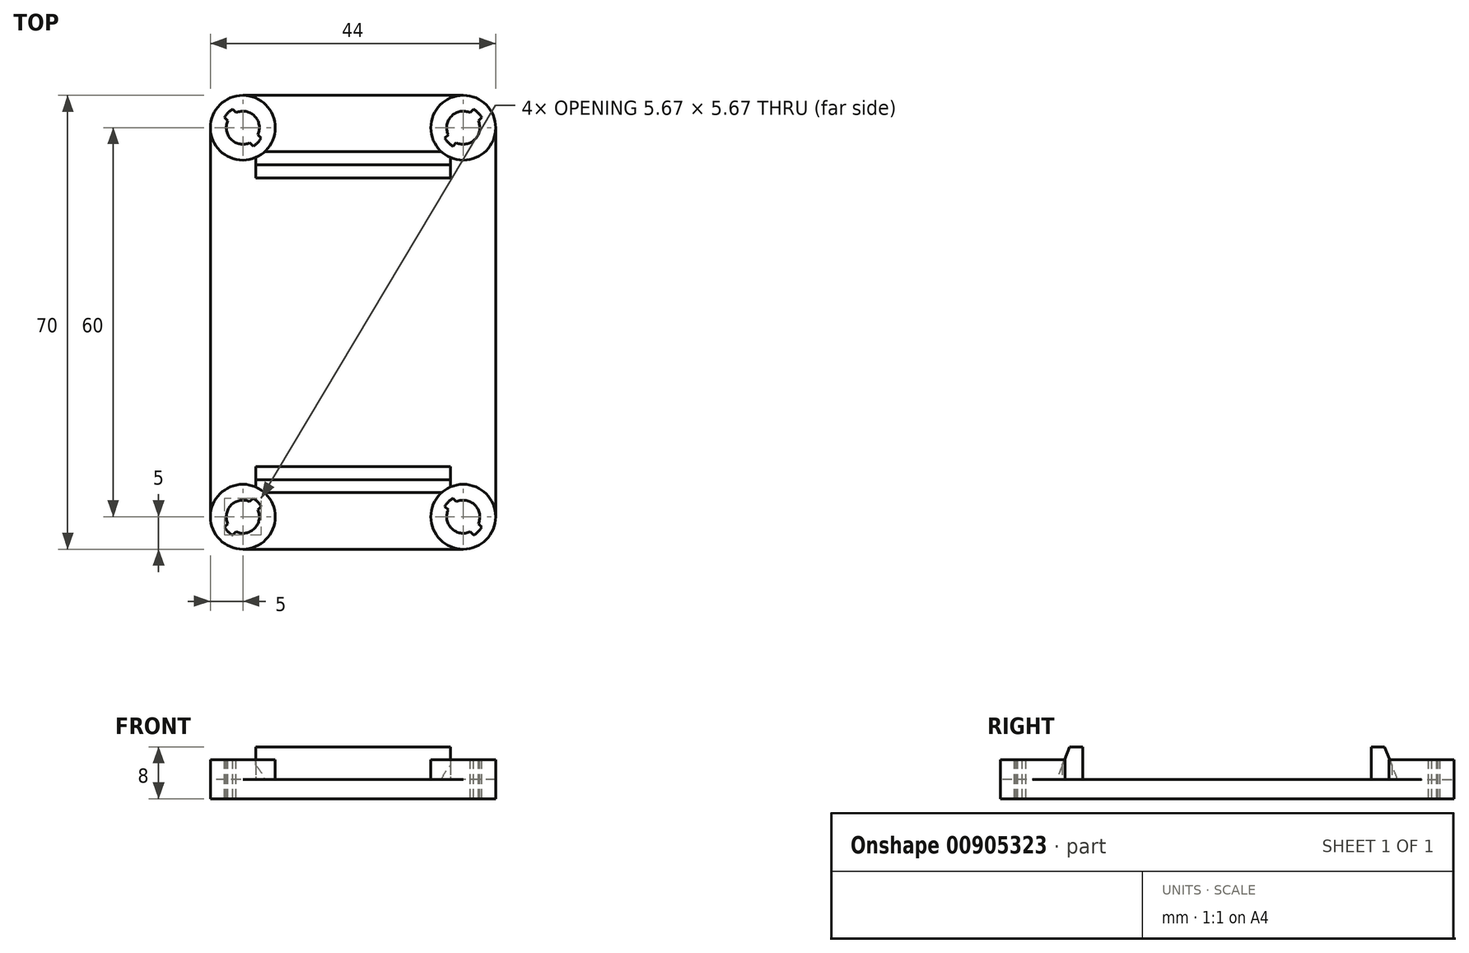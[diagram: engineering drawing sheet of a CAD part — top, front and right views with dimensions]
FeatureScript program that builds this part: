
annotation { "Feature Type Name" : "Feature", "Feature Type Description" : "" }
export const myFeature = defineFeature(function(context is Context, id is Id, definition is map)
    precondition{}
    {
        {
            var Q0;
            Q0=qCreatedBy(makeId("Top.planeOp"),FACE);
            var sketch = newSketch(context, id + "F0", { "sketchPlane" : qUnion([Q0])});
            skLineSegment(sketch, "E0.bottom", {"start": v(32.5, -22) * mm, "end": v(-32.5, -22) * mm, "construction": true});
            skLineSegment(sketch, "E0.top", {"start": v(32.5, 22) * mm, "end": v(-32.5, 22) * mm, "construction": true});
            skLineSegment(sketch, "E0.left", {"start": v(32.5, -22) * mm, "end": v(32.5, 22) * mm, "construction": true});
            skLineSegment(sketch, "E0.right", {"start": v(-32.5, -22) * mm, "end": v(-32.5, 22) * mm, "construction": true});
            skPoint(sketch, "E0.middle", {"position": v(0, 0) * mm});
            skLineSegment(sketch, "E1.bottom", {"start": v(17, -30) * mm, "end": v(-17, -30) * mm, "construction": true});
            skLineSegment(sketch, "E1.top", {"start": v(17, 30) * mm, "end": v(-17, 30) * mm, "construction": true});
            skLineSegment(sketch, "E1.left", {"start": v(17, -30) * mm, "end": v(17, 30) * mm, "construction": true});
            skLineSegment(sketch, "E1.right", {"start": v(-17, -30) * mm, "end": v(-17, 30) * mm, "construction": true});
            skLineSegment(sketch, "E2.0", {"start": v(17, 35) * mm, "end": v(-17, 35) * mm});
            skLineSegment(sketch, "E2.1", {"start": v(22, -30) * mm, "end": v(22, 30) * mm});
            skLineSegment(sketch, "E2.2", {"start": v(17, -35) * mm, "end": v(-17, -35) * mm});
            skLineSegment(sketch, "E2.3", {"start": v(-22, -30) * mm, "end": v(-22, 30) * mm});
            skPoint(sketch, "E3.visualSharp", {"position": v(-22, 35) * mm});
            skArc(sketch, "E3.filletArc", {"start": v(-17, 35) * mm, "mid": v(-20.54, 33.54) * mm, "end": v(-22, 30) * mm});
            skPoint(sketch, "E4.visualSharp", {"position": v(22, 35) * mm});
            skArc(sketch, "E4.filletArc", {"start": v(22, 30) * mm, "mid": v(20.54, 33.54) * mm, "end": v(17, 35) * mm});
            skPoint(sketch, "E5.visualSharp", {"position": v(22, -35) * mm});
            skArc(sketch, "E5.filletArc", {"start": v(17, -35) * mm, "mid": v(20.54, -33.54) * mm, "end": v(22, -30) * mm});
            skPoint(sketch, "E6.visualSharp", {"position": v(-22, -35) * mm});
            skArc(sketch, "E6.filletArc", {"start": v(-22, -30) * mm, "mid": v(-20.54, -33.54) * mm, "end": v(-17, -35) * mm});
            skSolve(sketch);
        }
        {
            var Q0;
            Q0 = qSketchRegion(id + "F0", true);
            extrude(context, id + "F1", {"entities" : qUnion([Q0]), "depth" : 3 * mm, "offsetDistance" : 25 * mm});
        }
        {
            var Q0;
            Q0=qCreatedBy(makeId("Top.planeOp"),FACE);
            var sketch = newSketch(context, id + "F2", { "sketchPlane" : qUnion([Q0])});
            skLineSegment(sketch, "E7.bottom", {"start": v(32.5, -22) * mm, "end": v(-32.5, -22) * mm, "construction": true});
            skLineSegment(sketch, "E7.top", {"start": v(32.5, 22) * mm, "end": v(-32.5, 22) * mm, "construction": true});
            skLineSegment(sketch, "E7.left", {"start": v(32.5, -22) * mm, "end": v(32.5, 22) * mm, "construction": true});
            skLineSegment(sketch, "E7.right", {"start": v(-32.5, -22) * mm, "end": v(-32.5, 22) * mm, "construction": true});
            skPoint(sketch, "E7.middle", {"position": v(0, 0) * mm});
            skLineSegment(sketch, "E8.bottom", {"start": v(17, -30) * mm, "end": v(-17, -30) * mm, "construction": true});
            skLineSegment(sketch, "E8.top", {"start": v(17, 30) * mm, "end": v(-17, 30) * mm, "construction": true});
            skLineSegment(sketch, "E8.left", {"start": v(17, -30) * mm, "end": v(17, 30) * mm, "construction": true});
            skLineSegment(sketch, "E8.right", {"start": v(-17, -30) * mm, "end": v(-17, 30) * mm, "construction": true});
            skLineSegment(sketch, "E9.0", {"start": v(22, 35) * mm, "end": v(-22, 35) * mm});
            skLineSegment(sketch, "E9.1", {"start": v(22, -35) * mm, "end": v(22, 35) * mm});
            skLineSegment(sketch, "E9.2", {"start": v(22, -35) * mm, "end": v(-22, -35) * mm});
            skLineSegment(sketch, "E9.3", {"start": v(-22, -35) * mm, "end": v(-22, 35) * mm});
            skCircle(sketch, "E10", {"center": v(-17, -30) * mm, "radius": 5 * mm});
            skCircle(sketch, "E11", {"center": v(17, -30) * mm, "radius": 5 * mm});
            skCircle(sketch, "E12", {"center": v(17, 30) * mm, "radius": 5 * mm});
            skCircle(sketch, "E13", {"center": v(-17, 30) * mm, "radius": 5 * mm});
            skSolve(sketch);
        }
        {
            var Q0;
            {var subQ0=sQuery(id+"F2.wireOp",EDGE,"E13");var subQ1=makeQuery(id+"F2.imprint","INTERSECT",VERTEX,{"derivedFrom":[sQuery(id+"F2.wireOp",EDGE,"E9.0"),subQ0]});Q0=makeQuery(id+"F2.imprint","IMPRINT",FACE,{"disambiguationData":[TD([[makeQuery(id+"F2.imprint","IMPRINT",EDGE,{"disambiguationData":[TD([[subQ1,-1.0]])],"derivedFrom":subQ0}),1.0]])]});}
            var Q1;
            {var subQ0=sQuery(id+"F2.wireOp",EDGE,"E12");var subQ1=makeQuery(id+"F2.imprint","INTERSECT",VERTEX,{"derivedFrom":[sQuery(id+"F2.wireOp",EDGE,"E9.0"),subQ0]});Q1=makeQuery(id+"F2.imprint","IMPRINT",FACE,{"disambiguationData":[TD([[makeQuery(id+"F2.imprint","IMPRINT",EDGE,{"disambiguationData":[TD([[subQ1,1.0]])],"derivedFrom":subQ0}),1.0]])]});}
            var Q2;
            {var subQ0=sQuery(id+"F2.wireOp",EDGE,"E11");var subQ1=makeQuery(id+"F2.imprint","INTERSECT",VERTEX,{"derivedFrom":[sQuery(id+"F2.wireOp",EDGE,"E9.1"),subQ0]});Q2=makeQuery(id+"F2.imprint","IMPRINT",FACE,{"disambiguationData":[TD([[makeQuery(id+"F2.imprint","IMPRINT",EDGE,{"disambiguationData":[TD([[subQ1,-1.0]])],"derivedFrom":subQ0}),1.0]])]});}
            var Q3;
            {var subQ0=sQuery(id+"F2.wireOp",EDGE,"E10");var subQ1=makeQuery(id+"F2.imprint","INTERSECT",VERTEX,{"derivedFrom":[sQuery(id+"F2.wireOp",EDGE,"E9.2"),subQ0]});Q3=makeQuery(id+"F2.imprint","IMPRINT",FACE,{"disambiguationData":[TD([[makeQuery(id+"F2.imprint","IMPRINT",EDGE,{"disambiguationData":[TD([[subQ1,1.0]])],"derivedFrom":subQ0}),1.0]])]});}
            extrude(context, id + "F3", {"entities" : qUnion([Q0, Q1, Q2, Q3]), "operationType" : NewBodyOperationType.ADD, "depth" : 6 * mm, "offsetDistance" : 25 * mm});
        }
        {
            var Q0;
            Q0=qCreatedBy(makeId("Top.planeOp"),FACE);
            var sketch = newSketch(context, id + "F4", { "sketchPlane" : qUnion([Q0])});
            skPoint(sketch, "E14.middle", {"position": v(0, 0) * mm});
            skLineSegment(sketch, "E15.top", {"start": v(17, 30) * mm, "end": v(-17, 30) * mm, "construction": true});
            skLineSegment(sketch, "E15.left", {"start": v(17, -30) * mm, "end": v(17, 30) * mm, "construction": true});
            skCircle(sketch, "E16", {"center": v(-17, -30) * mm, "radius": 2.55 * mm});
            skCircle(sketch, "E17", {"center": v(-17, -30) * mm, "radius": 3.25 * mm});
            skLineSegment(sketch, "E18.bottom", {"start": v(-13.82, -28.07) * mm, "end": v(-18.93, -33.18) * mm});
            skLineSegment(sketch, "E18.top", {"start": v(-15.07, -26.82) * mm, "end": v(-20.18, -31.93) * mm});
            skLineSegment(sketch, "E18.left", {"start": v(-13.82, -28.07) * mm, "end": v(-15.07, -26.82) * mm});
            skLineSegment(sketch, "E18.right", {"start": v(-18.93, -33.18) * mm, "end": v(-20.18, -31.93) * mm});
            skCircle(sketch, "E19", {"center": v(17, -30) * mm, "radius": 2.55 * mm});
            skCircle(sketch, "E20", {"center": v(17, -30) * mm, "radius": 3.25 * mm});
            skLineSegment(sketch, "E21.bottom", {"start": v(15.07, -26.82) * mm, "end": v(20.18, -31.93) * mm});
            skLineSegment(sketch, "E21.top", {"start": v(13.82, -28.07) * mm, "end": v(18.93, -33.18) * mm});
            skLineSegment(sketch, "E21.left", {"start": v(15.07, -26.82) * mm, "end": v(13.82, -28.07) * mm});
            skLineSegment(sketch, "E21.right", {"start": v(20.18, -31.93) * mm, "end": v(18.93, -33.18) * mm});
            skCircle(sketch, "E22", {"center": v(17, 30) * mm, "radius": 2.55 * mm});
            skCircle(sketch, "E23", {"center": v(17, 30) * mm, "radius": 3.25 * mm});
            skLineSegment(sketch, "E24.bottom", {"start": v(13.82, 28.07) * mm, "end": v(18.93, 33.18) * mm});
            skLineSegment(sketch, "E24.top", {"start": v(15.07, 26.82) * mm, "end": v(20.18, 31.93) * mm});
            skLineSegment(sketch, "E24.left", {"start": v(13.82, 28.07) * mm, "end": v(15.07, 26.82) * mm});
            skLineSegment(sketch, "E24.right", {"start": v(18.93, 33.18) * mm, "end": v(20.18, 31.93) * mm});
            skCircle(sketch, "E25", {"center": v(-17, 30) * mm, "radius": 2.55 * mm});
            skCircle(sketch, "E26", {"center": v(-17, 30) * mm, "radius": 3.25 * mm});
            skLineSegment(sketch, "E27.bottom", {"start": v(-15.07, 26.82) * mm, "end": v(-20.18, 31.93) * mm});
            skLineSegment(sketch, "E27.top", {"start": v(-13.82, 28.07) * mm, "end": v(-18.93, 33.18) * mm});
            skLineSegment(sketch, "E27.left", {"start": v(-15.07, 26.82) * mm, "end": v(-13.82, 28.07) * mm});
            skLineSegment(sketch, "E27.right", {"start": v(-20.18, 31.93) * mm, "end": v(-18.93, 33.18) * mm});
            skSolve(sketch);
        }
        {
            var Q0;
            {var subQ0=sQuery(id+"F4.wireOp",EDGE,"E18.bottom");var subQ1=sQuery(id+"F4.wireOp",EDGE,"E16");var subQ2=makeQuery(id+"F4.imprint","INTERSECT",VERTEX,{"disambiguationData":[OD(0.0)],"derivedFrom":[subQ1,subQ0]});Q0=makeQuery(id+"F4.imprint","IMPRINT",FACE,{"disambiguationData":[TD([[makeQuery(id+"F4.imprint","IMPRINT",EDGE,{"disambiguationData":[TD([[subQ2,1.0]])],"derivedFrom":subQ1}),1.0]])]});}
            var Q1;
            {var subQ0=sQuery(id+"F4.wireOp",EDGE,"E18.top");var subQ1=sQuery(id+"F4.wireOp",EDGE,"E16");var subQ2=makeQuery(id+"F4.imprint","INTERSECT",VERTEX,{"disambiguationData":[OD(0.0)],"derivedFrom":[subQ1,subQ0]});Q1=makeQuery(id+"F4.imprint","IMPRINT",FACE,{"disambiguationData":[TD([[makeQuery(id+"F4.imprint","IMPRINT",EDGE,{"disambiguationData":[TD([[subQ2,1.0]])],"derivedFrom":subQ1}),1.0]])]});}
            var Q2;
            {var subQ0=sQuery(id+"F4.wireOp",EDGE,"E18.top");var subQ1=sQuery(id+"F4.wireOp",EDGE,"E16");var subQ2=makeQuery(id+"F4.imprint","INTERSECT",VERTEX,{"disambiguationData":[OD(0.0)],"derivedFrom":[subQ1,subQ0]});Q2=makeQuery(id+"F4.imprint","IMPRINT",FACE,{"disambiguationData":[TD([[makeQuery(id+"F4.imprint","IMPRINT",EDGE,{"disambiguationData":[TD([[subQ2,-1.0]])],"derivedFrom":subQ1}),1.0]])]});}
            var Q3;
            {var subQ0=sQuery(id+"F4.wireOp",EDGE,"E18.top");var subQ1=sQuery(id+"F4.wireOp",EDGE,"E16");var subQ2=makeQuery(id+"F4.imprint","INTERSECT",VERTEX,{"disambiguationData":[OD(1.0)],"derivedFrom":[subQ1,subQ0]});Q3=makeQuery(id+"F4.imprint","IMPRINT",FACE,{"disambiguationData":[TD([[makeQuery(id+"F4.imprint","IMPRINT",EDGE,{"disambiguationData":[TD([[subQ2,-1.0]])],"derivedFrom":subQ1}),-1.0]])]});}
            var Q4;
            {var subQ0=sQuery(id+"F4.wireOp",EDGE,"E18.top");var subQ1=sQuery(id+"F4.wireOp",EDGE,"E16");var subQ2=makeQuery(id+"F4.imprint","INTERSECT",VERTEX,{"disambiguationData":[OD(0.0)],"derivedFrom":[subQ1,subQ0]});Q4=makeQuery(id+"F4.imprint","IMPRINT",FACE,{"disambiguationData":[TD([[makeQuery(id+"F4.imprint","IMPRINT",EDGE,{"disambiguationData":[TD([[subQ2,1.0]])],"derivedFrom":subQ1}),-1.0]])]});}
            var Q5;
            {var subQ0=sQuery(id+"F4.wireOp",EDGE,"E21.top");var subQ1=sQuery(id+"F4.wireOp",EDGE,"E19");var subQ2=makeQuery(id+"F4.imprint","INTERSECT",VERTEX,{"disambiguationData":[OD(0.0)],"derivedFrom":[subQ1,subQ0]});Q5=makeQuery(id+"F4.imprint","IMPRINT",FACE,{"disambiguationData":[TD([[makeQuery(id+"F4.imprint","IMPRINT",EDGE,{"disambiguationData":[TD([[subQ2,1.0]])],"derivedFrom":subQ1}),1.0]])]});}
            var Q6;
            {var subQ0=sQuery(id+"F4.wireOp",EDGE,"E21.top");var subQ1=sQuery(id+"F4.wireOp",EDGE,"E19");var subQ2=makeQuery(id+"F4.imprint","INTERSECT",VERTEX,{"disambiguationData":[OD(1.0)],"derivedFrom":[subQ1,subQ0]});Q6=makeQuery(id+"F4.imprint","IMPRINT",FACE,{"disambiguationData":[TD([[makeQuery(id+"F4.imprint","IMPRINT",EDGE,{"disambiguationData":[TD([[subQ2,-1.0]])],"derivedFrom":subQ1}),-1.0]])]});}
            var Q7;
            {var subQ0=sQuery(id+"F4.wireOp",EDGE,"E21.top");var subQ1=sQuery(id+"F4.wireOp",EDGE,"E19");var subQ2=makeQuery(id+"F4.imprint","INTERSECT",VERTEX,{"disambiguationData":[OD(0.0)],"derivedFrom":[subQ1,subQ0]});Q7=makeQuery(id+"F4.imprint","IMPRINT",FACE,{"disambiguationData":[TD([[makeQuery(id+"F4.imprint","IMPRINT",EDGE,{"disambiguationData":[TD([[subQ2,-1.0]])],"derivedFrom":subQ1}),1.0]])]});}
            var Q8;
            {var subQ0=sQuery(id+"F4.wireOp",EDGE,"E21.bottom");var subQ1=sQuery(id+"F4.wireOp",EDGE,"E19");var subQ2=makeQuery(id+"F4.imprint","INTERSECT",VERTEX,{"disambiguationData":[OD(0.0)],"derivedFrom":[subQ1,subQ0]});Q8=makeQuery(id+"F4.imprint","IMPRINT",FACE,{"disambiguationData":[TD([[makeQuery(id+"F4.imprint","IMPRINT",EDGE,{"disambiguationData":[TD([[subQ2,1.0]])],"derivedFrom":subQ1}),1.0]])]});}
            var Q9;
            {var subQ0=sQuery(id+"F4.wireOp",EDGE,"E21.top");var subQ1=sQuery(id+"F4.wireOp",EDGE,"E19");var subQ2=makeQuery(id+"F4.imprint","INTERSECT",VERTEX,{"disambiguationData":[OD(0.0)],"derivedFrom":[subQ1,subQ0]});Q9=makeQuery(id+"F4.imprint","IMPRINT",FACE,{"disambiguationData":[TD([[makeQuery(id+"F4.imprint","IMPRINT",EDGE,{"disambiguationData":[TD([[subQ2,1.0]])],"derivedFrom":subQ1}),-1.0]])]});}
            var Q10;
            {var subQ0=sQuery(id+"F4.wireOp",EDGE,"E24.top");var subQ1=sQuery(id+"F4.wireOp",EDGE,"E22");var subQ2=makeQuery(id+"F4.imprint","INTERSECT",VERTEX,{"disambiguationData":[OD(0.0)],"derivedFrom":[subQ1,subQ0]});Q10=makeQuery(id+"F4.imprint","IMPRINT",FACE,{"disambiguationData":[TD([[makeQuery(id+"F4.imprint","IMPRINT",EDGE,{"disambiguationData":[TD([[subQ2,1.0]])],"derivedFrom":subQ1}),1.0]])]});}
            var Q11;
            {var subQ0=sQuery(id+"F4.wireOp",EDGE,"E24.top");var subQ1=sQuery(id+"F4.wireOp",EDGE,"E22");var subQ2=makeQuery(id+"F4.imprint","INTERSECT",VERTEX,{"disambiguationData":[OD(0.0)],"derivedFrom":[subQ1,subQ0]});Q11=makeQuery(id+"F4.imprint","IMPRINT",FACE,{"disambiguationData":[TD([[makeQuery(id+"F4.imprint","IMPRINT",EDGE,{"disambiguationData":[TD([[subQ2,-1.0]])],"derivedFrom":subQ1}),1.0]])]});}
            var Q12;
            {var subQ0=sQuery(id+"F4.wireOp",EDGE,"E24.bottom");var subQ1=sQuery(id+"F4.wireOp",EDGE,"E22");var subQ2=makeQuery(id+"F4.imprint","INTERSECT",VERTEX,{"disambiguationData":[OD(0.0)],"derivedFrom":[subQ1,subQ0]});Q12=makeQuery(id+"F4.imprint","IMPRINT",FACE,{"disambiguationData":[TD([[makeQuery(id+"F4.imprint","IMPRINT",EDGE,{"disambiguationData":[TD([[subQ2,1.0]])],"derivedFrom":subQ1}),1.0]])]});}
            var Q13;
            {var subQ0=sQuery(id+"F4.wireOp",EDGE,"E24.top");var subQ1=sQuery(id+"F4.wireOp",EDGE,"E22");var subQ2=makeQuery(id+"F4.imprint","INTERSECT",VERTEX,{"disambiguationData":[OD(1.0)],"derivedFrom":[subQ1,subQ0]});Q13=makeQuery(id+"F4.imprint","IMPRINT",FACE,{"disambiguationData":[TD([[makeQuery(id+"F4.imprint","IMPRINT",EDGE,{"disambiguationData":[TD([[subQ2,-1.0]])],"derivedFrom":subQ1}),-1.0]])]});}
            var Q14;
            {var subQ0=sQuery(id+"F4.wireOp",EDGE,"E24.top");var subQ1=sQuery(id+"F4.wireOp",EDGE,"E22");var subQ2=makeQuery(id+"F4.imprint","INTERSECT",VERTEX,{"disambiguationData":[OD(0.0)],"derivedFrom":[subQ1,subQ0]});Q14=makeQuery(id+"F4.imprint","IMPRINT",FACE,{"disambiguationData":[TD([[makeQuery(id+"F4.imprint","IMPRINT",EDGE,{"disambiguationData":[TD([[subQ2,1.0]])],"derivedFrom":subQ1}),-1.0]])]});}
            var Q15;
            {var subQ0=sQuery(id+"F4.wireOp",EDGE,"E27.top");var subQ1=sQuery(id+"F4.wireOp",EDGE,"E25");var subQ2=makeQuery(id+"F4.imprint","INTERSECT",VERTEX,{"disambiguationData":[OD(0.0)],"derivedFrom":[subQ1,subQ0]});Q15=makeQuery(id+"F4.imprint","IMPRINT",FACE,{"disambiguationData":[TD([[makeQuery(id+"F4.imprint","IMPRINT",EDGE,{"disambiguationData":[TD([[subQ2,1.0]])],"derivedFrom":subQ1}),1.0]])]});}
            var Q16;
            {var subQ0=sQuery(id+"F4.wireOp",EDGE,"E27.top");var subQ1=sQuery(id+"F4.wireOp",EDGE,"E25");var subQ2=makeQuery(id+"F4.imprint","INTERSECT",VERTEX,{"disambiguationData":[OD(0.0)],"derivedFrom":[subQ1,subQ0]});Q16=makeQuery(id+"F4.imprint","IMPRINT",FACE,{"disambiguationData":[TD([[makeQuery(id+"F4.imprint","IMPRINT",EDGE,{"disambiguationData":[TD([[subQ2,-1.0]])],"derivedFrom":subQ1}),1.0]])]});}
            var Q17;
            {var subQ0=sQuery(id+"F4.wireOp",EDGE,"E27.top");var subQ1=sQuery(id+"F4.wireOp",EDGE,"E25");var subQ2=makeQuery(id+"F4.imprint","INTERSECT",VERTEX,{"disambiguationData":[OD(0.0)],"derivedFrom":[subQ1,subQ0]});Q17=makeQuery(id+"F4.imprint","IMPRINT",FACE,{"disambiguationData":[TD([[makeQuery(id+"F4.imprint","IMPRINT",EDGE,{"disambiguationData":[TD([[subQ2,1.0]])],"derivedFrom":subQ1}),-1.0]])]});}
            var Q18;
            {var subQ0=sQuery(id+"F4.wireOp",EDGE,"E27.bottom");var subQ1=sQuery(id+"F4.wireOp",EDGE,"E25");var subQ2=makeQuery(id+"F4.imprint","INTERSECT",VERTEX,{"disambiguationData":[OD(0.0)],"derivedFrom":[subQ1,subQ0]});Q18=makeQuery(id+"F4.imprint","IMPRINT",FACE,{"disambiguationData":[TD([[makeQuery(id+"F4.imprint","IMPRINT",EDGE,{"disambiguationData":[TD([[subQ2,1.0]])],"derivedFrom":subQ1}),1.0]])]});}
            var Q19;
            {var subQ0=sQuery(id+"F4.wireOp",EDGE,"E27.top");var subQ1=sQuery(id+"F4.wireOp",EDGE,"E25");var subQ2=makeQuery(id+"F4.imprint","INTERSECT",VERTEX,{"disambiguationData":[OD(1.0)],"derivedFrom":[subQ1,subQ0]});Q19=makeQuery(id+"F4.imprint","IMPRINT",FACE,{"disambiguationData":[TD([[makeQuery(id+"F4.imprint","IMPRINT",EDGE,{"disambiguationData":[TD([[subQ2,-1.0]])],"derivedFrom":subQ1}),-1.0]])]});}
            extrude(context, id + "F5", {"entities" : qUnion([Q0, Q1, Q2, Q3, Q4, Q5, Q6, Q7, Q8, Q9, Q10, Q11, Q12, Q13, Q14, Q15, Q16, Q17, Q18, Q19]), "operationType" : NewBodyOperationType.REMOVE, "endBound" : BoundingType.SYMMETRIC, "oppositeDirection" : true, "depth" : 25 * mm, "offsetDistance" : 25 * mm});
        }
        {
            var Q0;
            Q0=qCreatedBy(makeId("Top.planeOp"),FACE);
            var sketch = newSketch(context, id + "F6", { "sketchPlane" : qUnion([Q0])});
            skLineSegment(sketch, "E28.bottom", {"start": v(15, 22.25) * mm, "end": v(-15, 22.25) * mm, "construction": true});
            skPoint(sketch, "E28.middle", {"position": v(0, 0) * mm});
            skPoint(sketch, "E29.middle", {"position": v(0, 22.25) * mm});
            skLineSegment(sketch, "E30", {"start": v(-15, 22.25) * mm, "end": v(15, 22.25) * mm});
            skPoint(sketch, "E31.MirrorP", {"position": v(0, -22.25) * mm});
            skLineSegment(sketch, "E32.top", {"start": v(-15, 24.29) * mm, "end": v(15, 24.29) * mm});
            skLineSegment(sketch, "E32.left", {"start": v(-15, 22.25) * mm, "end": v(-15, 24.29) * mm});
            skLineSegment(sketch, "E32.right", {"start": v(15, 22.25) * mm, "end": v(15, 24.29) * mm});
            skLineSegment(sketch, "E33.MirrorCS", {"start": v(-15, -22.25) * mm, "end": v(15, -22.25) * mm});
            skLineSegment(sketch, "E34.MirrorCS", {"start": v(-15, -22.25) * mm, "end": v(-15, -24.29) * mm});
            skLineSegment(sketch, "E35.MirrorCS", {"start": v(15, -22.25) * mm, "end": v(15, -24.29) * mm});
            skLineSegment(sketch, "E36.MirrorCS", {"start": v(-15, -24.29) * mm, "end": v(15, -24.29) * mm});
            skLineSegment(sketch, "E37.MirrorCS", {"start": v(15, -22.25) * mm, "end": v(-15, -22.25) * mm, "construction": true});
            skSolve(sketch);
        }
        {
            var Q0;
            Q0 = qSketchRegion(id + "F6", true);
            extrude(context, id + "F7", {"entities" : qUnion([Q0]), "operationType" : NewBodyOperationType.ADD, "depth" : 8 * mm, "offsetDistance" : 25 * mm});
        }
        {
            var Q0;
            Q0=makeQuery(id+"F7.boolean.opBoolean","INTERSECT",EDGE,{"derivedFrom":[makeQuery(id+"F1.opExtrude","CAP_FACE",FACE,{"disambiguationData":[OSD([sQuery(id+"F0.wireOp",EDGE,"E2.0"),sQuery(id+"F0.wireOp",EDGE,"E2.1"),sQuery(id+"F0.wireOp",EDGE,"E2.2"),sQuery(id+"F0.wireOp",EDGE,"E2.3"),sQuery(id+"F0.wireOp",EDGE,"E3.filletArc"),sQuery(id+"F0.wireOp",EDGE,"E4.filletArc"),sQuery(id+"F0.wireOp",EDGE,"E5.filletArc"),sQuery(id+"F0.wireOp",EDGE,"E6.filletArc")])],"isStart":false}),makeQuery(id+"F7.opExtrude","SWEPT_FACE",FACE,{"disambiguationData":[OSD([sQuery(id+"F6.wireOp",EDGE,"E32.top")])]})]});
            var Q1;
            Q1=makeQuery(id+"F7.boolean.opBoolean","INTERSECT",EDGE,{"derivedFrom":[makeQuery(id+"F1.opExtrude","CAP_FACE",FACE,{"disambiguationData":[OSD([sQuery(id+"F0.wireOp",EDGE,"E2.0"),sQuery(id+"F0.wireOp",EDGE,"E2.1"),sQuery(id+"F0.wireOp",EDGE,"E2.2"),sQuery(id+"F0.wireOp",EDGE,"E2.3"),sQuery(id+"F0.wireOp",EDGE,"E3.filletArc"),sQuery(id+"F0.wireOp",EDGE,"E4.filletArc"),sQuery(id+"F0.wireOp",EDGE,"E5.filletArc"),sQuery(id+"F0.wireOp",EDGE,"E6.filletArc")])],"isStart":false}),makeQuery(id+"F7.opExtrude","SWEPT_FACE",FACE,{"disambiguationData":[OSD([sQuery(id+"F6.wireOp",EDGE,"E36.MirrorCS")])]})]});
            chamfer(context, id + "F8", {"entities" : qUnion([Q0, Q1]), "chamferType" : ChamferType.TWO_OFFSETS, "width1" : 5 * mm, "oppositeDirection" : false, "width2" : 2 * mm, "tangentPropagation" : true});
        }
    });
